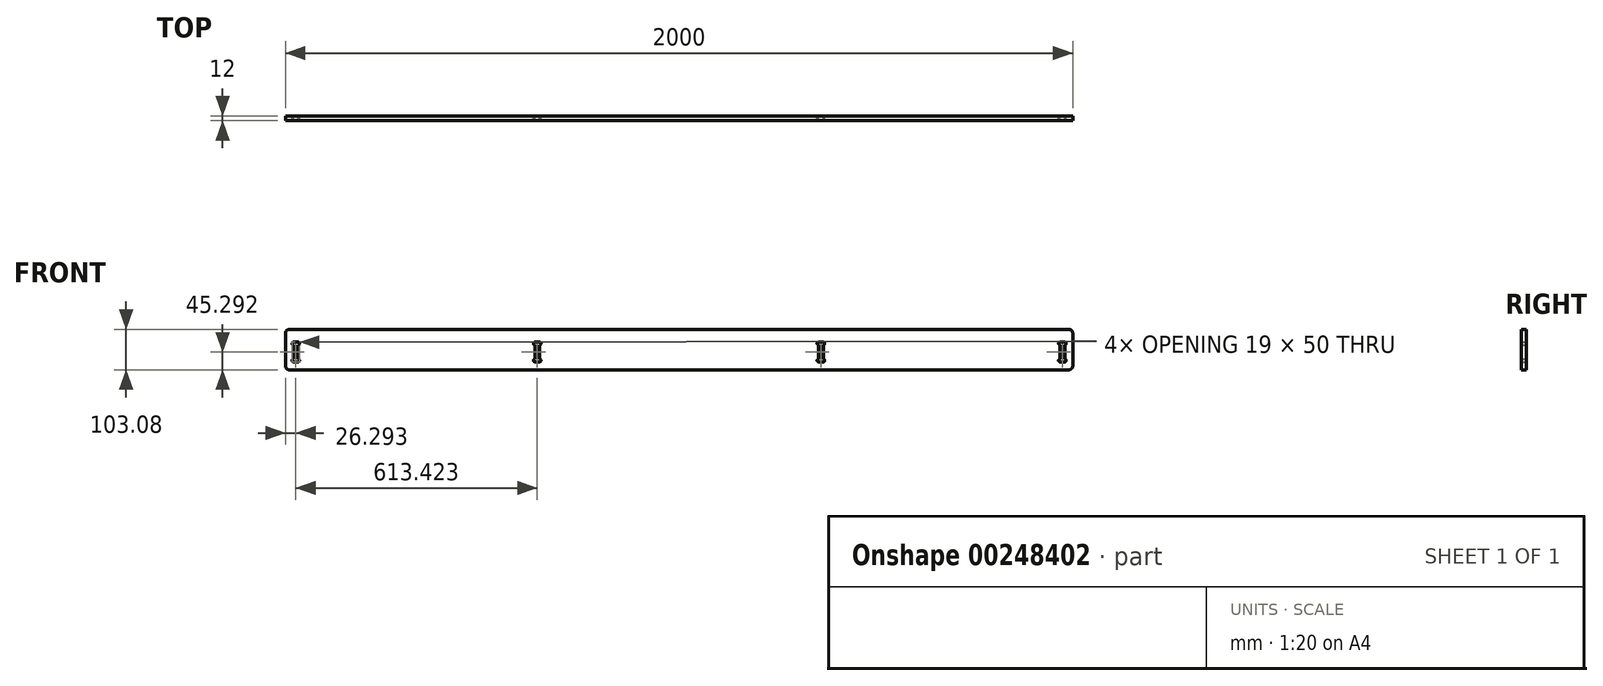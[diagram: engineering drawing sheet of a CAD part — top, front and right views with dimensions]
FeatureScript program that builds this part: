
annotation { "Feature Type Name" : "Feature", "Feature Type Description" : "" }
export const myFeature = defineFeature(function(context is Context, id is Id, definition is map)
    precondition{}
    {
        {
            var Q0;
            Q0=qCreatedBy(makeId("Front.planeOp"),FACE);
            var sketch = newSketch(context, id + "F0", { "sketchPlane" : qUnion([Q0])});
            skLineSegment(sketch, "E0.bottom", {"start": v(-931.2, 27.38) * mm, "end": v(1048.8, 27.38) * mm});
            skLineSegment(sketch, "E0.top", {"start": v(-931.2, -75.7) * mm, "end": v(1048.8, -75.7) * mm});
            skLineSegment(sketch, "E0.left", {"start": v(-941.2, 17.38) * mm, "end": v(-941.2, -65.7) * mm});
            skLineSegment(sketch, "E0.right", {"start": v(1058.8, 17.38) * mm, "end": v(1058.8, -65.7) * mm});
            skPoint(sketch, "E1.visualSharp", {"position": v(-941.2, 27.38) * mm});
            skArc(sketch, "E1.filletArc", {"start": v(-931.2, 27.38) * mm, "mid": v(-938.27, 24.45) * mm, "end": v(-941.2, 17.38) * mm});
            skPoint(sketch, "E2.visualSharp", {"position": v(-941.2, -75.7) * mm});
            skArc(sketch, "E2.filletArc", {"start": v(-941.2, -65.7) * mm, "mid": v(-938.27, -72.77) * mm, "end": v(-931.2, -75.7) * mm});
            skPoint(sketch, "E3.visualSharp", {"position": v(1058.8, 27.38) * mm});
            skArc(sketch, "E3.filletArc", {"start": v(1058.8, 17.38) * mm, "mid": v(1055.88, 24.45) * mm, "end": v(1048.8, 27.38) * mm});
            skPoint(sketch, "E4.visualSharp", {"position": v(1058.8, -75.7) * mm});
            skArc(sketch, "E4.filletArc", {"start": v(1048.8, -75.7) * mm, "mid": v(1055.88, -72.77) * mm, "end": v(1058.8, -65.7) * mm});
            skLineSegment(sketch, "E5.top", {"start": v(-902.9, -75.7) * mm, "end": v(-920.9, -75.7) * mm});
            skLineSegment(sketch, "E6.top", {"start": v(1038.52, -75.7) * mm, "end": v(1058.8, -75.7) * mm, "construction": true});
            skLineSegment(sketch, "E6.right", {"start": v(1058.8, -5.4) * mm, "end": v(1058.8, -75.7) * mm, "construction": true});
            skLineSegment(sketch, "E7", {"start": v(-920.9, -5.4) * mm, "end": v(-908.9, -5.4) * mm});
            skLineSegment(sketch, "E8", {"start": v(-920.9, -55.4) * mm, "end": v(-908.9, -55.4) * mm});
            skArc(sketch, "E9", {"start": v(-908.9, -55.4) * mm, "mid": v(-905.4, -51.9) * mm, "end": v(-908.9, -48.4) * mm});
            skArc(sketch, "E10", {"start": v(-920.9, -48.4) * mm, "mid": v(-924.4, -51.9) * mm, "end": v(-920.9, -55.4) * mm});
            skArc(sketch, "E11", {"start": v(-908.9, -12.4) * mm, "mid": v(-905.4, -8.9) * mm, "end": v(-908.9, -5.4) * mm});
            skArc(sketch, "E12", {"start": v(-920.9, -5.4) * mm, "mid": v(-924.4, -8.9) * mm, "end": v(-920.9, -12.4) * mm});
            skLineSegment(sketch, "E13", {"start": v(-920.9, -55.4) * mm, "end": v(-920.9, -55.48) * mm});
            skLineSegment(sketch, "E14.trimOffspring", {"start": v(-920.9, -12.4) * mm, "end": v(-920.9, -48.4) * mm});
            skLineSegment(sketch, "E15.0", {"start": v(-908.9, -12.4) * mm, "end": v(-908.9, -48.4) * mm});
            skLineSegment(sketch, "E16.0", {"start": v(58.8, -5.4) * mm, "end": v(58.8, -55.48) * mm, "construction": true});
            skLineSegment(sketch, "E17.MirrorCS", {"start": v(1038.52, -12.4) * mm, "end": v(1038.52, -48.4) * mm});
            skArc(sketch, "E18.MirrorCS", {"start": v(1038.52, -5.4) * mm, "mid": v(1042.02, -8.9) * mm, "end": v(1038.52, -12.4) * mm});
            skLineSegment(sketch, "E19.MirrorCS", {"start": v(1038.52, -5.4) * mm, "end": v(1026.52, -5.4) * mm});
            skArc(sketch, "E20.MirrorCS", {"start": v(1026.52, -12.4) * mm, "mid": v(1023.02, -8.9) * mm, "end": v(1026.52, -5.4) * mm});
            skLineSegment(sketch, "E21.MirrorCS", {"start": v(1026.52, -12.4) * mm, "end": v(1026.52, -48.4) * mm});
            skArc(sketch, "E22.MirrorCS", {"start": v(1026.52, -55.4) * mm, "mid": v(1023.02, -51.9) * mm, "end": v(1026.52, -48.4) * mm});
            skLineSegment(sketch, "E23.MirrorCS", {"start": v(1038.52, -55.4) * mm, "end": v(1026.52, -55.4) * mm});
            skArc(sketch, "E24.MirrorCS", {"start": v(1038.52, -48.4) * mm, "mid": v(1042.02, -51.9) * mm, "end": v(1038.52, -55.4) * mm});
            skLineSegment(sketch, "E25.0", {"start": v(-608.2, 17.38) * mm, "end": v(-608.2, -65.7) * mm, "construction": true});
            skLineSegment(sketch, "E26.MirrorCS", {"start": v(-295.48, -55.4) * mm, "end": v(-295.48, -55.48) * mm});
            skArc(sketch, "E27.MirrorCS", {"start": v(-295.48, -48.4) * mm, "mid": v(-291.98, -51.9) * mm, "end": v(-295.48, -55.4) * mm});
            skArc(sketch, "E28.MirrorCS", {"start": v(-295.48, -5.4) * mm, "mid": v(-291.98, -8.9) * mm, "end": v(-295.48, -12.4) * mm});
            skArc(sketch, "E29.MirrorCS", {"start": v(-307.48, -12.4) * mm, "mid": v(-310.98, -8.9) * mm, "end": v(-307.48, -5.4) * mm});
            skArc(sketch, "E30.MirrorCS", {"start": v(-307.48, -55.4) * mm, "mid": v(-310.98, -51.9) * mm, "end": v(-307.48, -48.4) * mm});
            skLineSegment(sketch, "E31.MirrorCS", {"start": v(-295.48, -5.4) * mm, "end": v(-307.48, -5.4) * mm});
            skLineSegment(sketch, "E32.MirrorCS", {"start": v(-307.48, -12.4) * mm, "end": v(-307.48, -48.4) * mm});
            skLineSegment(sketch, "E33.MirrorCS", {"start": v(-295.48, -12.4) * mm, "end": v(-295.48, -48.4) * mm});
            skLineSegment(sketch, "E34.MirrorCS", {"start": v(-295.48, -55.4) * mm, "end": v(-307.48, -55.4) * mm});
            skLineSegment(sketch, "E35.MirrorCS", {"start": v(413.1, -55.4) * mm, "end": v(413.1, -55.48) * mm});
            skArc(sketch, "E36.MirrorCS", {"start": v(413.1, -48.4) * mm, "mid": v(409.6, -51.9) * mm, "end": v(413.1, -55.4) * mm});
            skLineSegment(sketch, "E37.MirrorCS", {"start": v(413.1, -55.4) * mm, "end": v(425.1, -55.4) * mm});
            skArc(sketch, "E38.MirrorCS", {"start": v(425.1, -12.4) * mm, "mid": v(428.6, -8.9) * mm, "end": v(425.1, -5.4) * mm});
            skArc(sketch, "E39.MirrorCS", {"start": v(413.1, -5.4) * mm, "mid": v(409.6, -8.9) * mm, "end": v(413.1, -12.4) * mm});
            skArc(sketch, "E40.MirrorCS", {"start": v(425.1, -55.4) * mm, "mid": v(428.6, -51.9) * mm, "end": v(425.1, -48.4) * mm});
            skLineSegment(sketch, "E41.MirrorCS", {"start": v(413.1, -5.4) * mm, "end": v(425.1, -5.4) * mm});
            skLineSegment(sketch, "E42.MirrorCS", {"start": v(425.1, -12.4) * mm, "end": v(425.1, -48.4) * mm});
            skLineSegment(sketch, "E43.MirrorCS", {"start": v(413.1, -12.4) * mm, "end": v(413.1, -48.4) * mm});
            skSolve(sketch);
        }
        {
            var Q0;
            Q0=makeQuery(id+"F0.imprint","IMPRINT",FACE,{"disambiguationData":[TD([[makeQuery(id+"F0.imprint","IMPRINT",EDGE,{"derivedFrom":sQuery(id+"F0.wireOp",EDGE,"E0.bottom")}),-1.0]])]});
            extrude(context, id + "F1", {"entities" : qUnion([Q0]), "depth" : 12 * mm});
        }
    });
